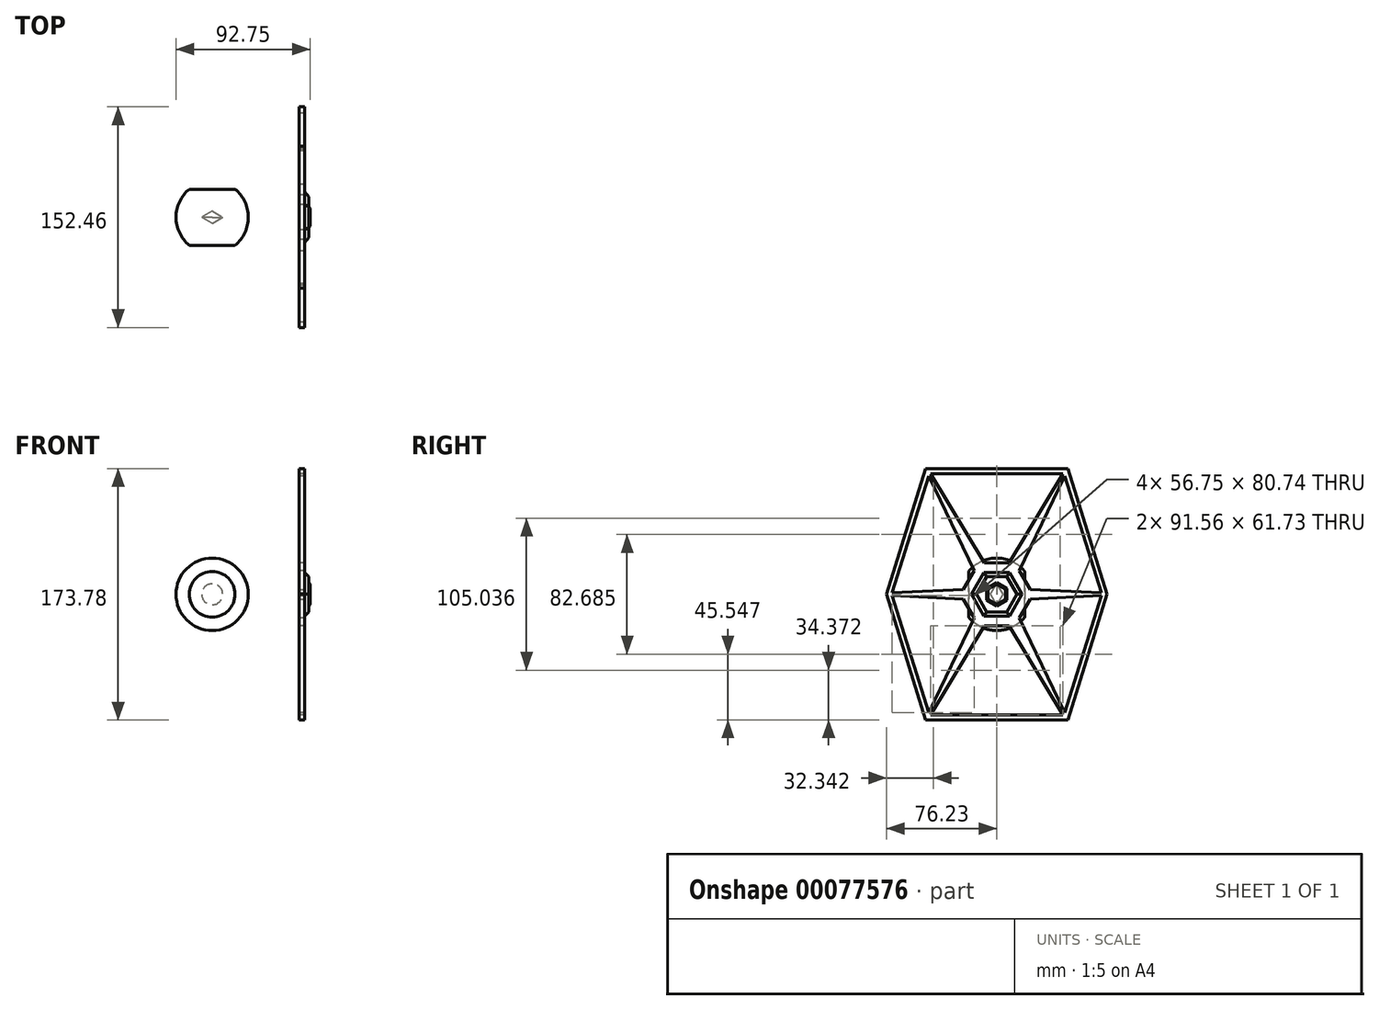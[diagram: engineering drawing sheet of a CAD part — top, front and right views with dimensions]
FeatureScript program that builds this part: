
annotation { "Feature Type Name" : "Feature", "Feature Type Description" : "" }
export const myFeature = defineFeature(function(context is Context, id is Id, definition is map)
    precondition{}
    {
        {
            var Q0;
            Q0=qCreatedBy(makeId("Right.planeOp"),FACE);
            var sketch = newSketch(context, id + "F0", { "sketchPlane" : qUnion([Q0])});
            skLineSegment(sketch, "E0", {"start": v(-19.38, 15.8) * mm, "end": v(-19.38, 0) * mm});
            skLineSegment(sketch, "E1", {"start": v(19.38, 15.8) * mm, "end": v(19.38, 0) * mm});
            skArc(sketch, "E2.trimOffspring", {"start": v(19.38, 15.8) * mm, "mid": v(0, 25) * mm, "end": v(-19.38, 15.8) * mm});
            skPoint(sketch, "E3.end.orphan", {"position": v(19.38, -15.72) * mm});
            skPoint(sketch, "E3.start.orphan", {"position": v(-19.38, -16.12) * mm});
            skLineSegment(sketch, "E4", {"start": v(0, 0) * mm, "end": v(0, 86.89) * mm, "construction": true});
            skPoint(sketch, "E4.endSnap0", {"position": v(0, 25) * mm});
            skLineSegment(sketch, "E5", {"start": v(0, 86.89) * mm, "end": v(49.08, 86.89) * mm});
            skLineSegment(sketch, "E6", {"start": v(49.08, 86.89) * mm, "end": v(76.23, 0) * mm});
            skLineSegment(sketch, "E7", {"start": v(0, 83.39) * mm, "end": v(45.78, 83.39) * mm});
            skLineSegment(sketch, "E8", {"start": v(45.78, 83.39) * mm, "end": v(-4.38, 0) * mm});
            skLineSegment(sketch, "E9.0", {"start": v(47.03, 81.71) * mm, "end": v(72.57, 0) * mm});
            skLineSegment(sketch, "E10", {"start": v(76.23, 0) * mm, "end": v(0, 0) * mm, "construction": true});
            skLineSegment(sketch, "E11", {"start": v(0, 0) * mm, "end": v(-19.38, 0) * mm});
            skLineSegment(sketch, "E12", {"start": v(0, 0) * mm, "end": v(19.38, 0) * mm});
            skPoint(sketch, "E13.orphan", {"position": v(19.38, 0.04) * mm});
            skPoint(sketch, "E14.orphan", {"position": v(-19.38, -0.16) * mm});
            skLineSegment(sketch, "E15", {"start": v(47.03, 81.71) * mm, "end": v(7.57, 0) * mm});
            skLineSegment(sketch, "E16.MirrorCS", {"start": v(0, 86.89) * mm, "end": v(-49.08, 86.89) * mm});
            skLineSegment(sketch, "E17.MirrorCS", {"start": v(0, 83.39) * mm, "end": v(-45.78, 83.39) * mm});
            skLineSegment(sketch, "E18.MirrorCS", {"start": v(-49.08, 86.89) * mm, "end": v(-76.23, 0) * mm});
            skLineSegment(sketch, "E19.MirrorCS", {"start": v(-47.03, 81.71) * mm, "end": v(-72.57, 0) * mm});
            skLineSegment(sketch, "E20.MirrorCS", {"start": v(-45.78, 83.39) * mm, "end": v(4.38, 0) * mm});
            skLineSegment(sketch, "E21.MirrorCS", {"start": v(-47.03, 81.71) * mm, "end": v(-7.57, 0) * mm});
            skLineSegment(sketch, "E22.MirrorCS", {"start": v(-76.23, 0) * mm, "end": v(0, 0) * mm, "construction": true});
            skLineSegment(sketch, "E23.MirrorCS", {"start": v(47.03, -81.71) * mm, "end": v(72.57, 0) * mm});
            skLineSegment(sketch, "E24.MirrorCS", {"start": v(49.08, -86.89) * mm, "end": v(76.23, 0) * mm});
            skLineSegment(sketch, "E25.MirrorCS", {"start": v(47.03, -81.71) * mm, "end": v(7.57, 0) * mm});
            skLineSegment(sketch, "E26.MirrorCS", {"start": v(45.78, -83.39) * mm, "end": v(-4.38, 0) * mm});
            skLineSegment(sketch, "E27.MirrorCS", {"start": v(0, -83.39) * mm, "end": v(45.78, -83.39) * mm});
            skLineSegment(sketch, "E28.MirrorCS", {"start": v(0, -86.89) * mm, "end": v(49.08, -86.89) * mm});
            skLineSegment(sketch, "E29.MirrorCS", {"start": v(0, -86.89) * mm, "end": v(-49.08, -86.89) * mm});
            skLineSegment(sketch, "E30.MirrorCS", {"start": v(0, -83.39) * mm, "end": v(-45.78, -83.39) * mm});
            skLineSegment(sketch, "E31.MirrorCS", {"start": v(-45.78, -83.39) * mm, "end": v(4.38, 0) * mm});
            skLineSegment(sketch, "E32.MirrorCS", {"start": v(-47.03, -81.71) * mm, "end": v(-7.57, 0) * mm});
            skLineSegment(sketch, "E33.MirrorCS", {"start": v(-47.03, -81.71) * mm, "end": v(-72.57, 0) * mm});
            skLineSegment(sketch, "E34.MirrorCS", {"start": v(-49.08, -86.89) * mm, "end": v(-76.23, 0) * mm});
            skSolve(sketch);
        }
        {
            var Q0;
            {var subQ6=sQuery(id+"F0.wireOp",EDGE,"E0");Q0=makeQuery(id+"F0.imprint","IMPRINT",FACE,{"disambiguationData":[TD([[makeQuery(id+"F0.imprint","IMPRINT",EDGE,{"derivedFrom":subQ6}),1.0]])]});}
            var Q1;
            {var subQ6=sQuery(id+"F0.wireOp",EDGE,"E20.MirrorCS");var subQ8=sQuery(id+"F0.wireOp",EDGE,"E2.trimOffspring");var subQ9=makeQuery(id+"F0.imprint","INTERSECT",VERTEX,{"derivedFrom":[subQ8,subQ6]});Q1=makeQuery(id+"F0.imprint","IMPRINT",FACE,{"disambiguationData":[TD([[makeQuery(id+"F0.imprint","IMPRINT",EDGE,{"disambiguationData":[TD([[subQ9,-1.0]])],"derivedFrom":subQ8}),1.0]])]});}
            var Q2;
            {var subQ0=sQuery(id+"F0.wireOp",EDGE,"E8");var subQ1=sQuery(id+"F0.wireOp",EDGE,"E2.trimOffspring");var subQ2=makeQuery(id+"F0.imprint","INTERSECT",VERTEX,{"derivedFrom":[subQ1,subQ0]});Q2=makeQuery(id+"F0.imprint","IMPRINT",FACE,{"disambiguationData":[TD([[makeQuery(id+"F0.imprint","IMPRINT",EDGE,{"disambiguationData":[TD([[subQ2,-1.0]])],"derivedFrom":subQ1}),1.0]])]});}
            var Q3;
            {var subQ1=sQuery(id+"F0.wireOp",EDGE,"E2.trimOffspring");var subQ5=sQuery(id+"F0.wireOp",EDGE,"E15");var subQ10=makeQuery(id+"F0.imprint","INTERSECT",VERTEX,{"derivedFrom":[subQ1,subQ5]});Q3=makeQuery(id+"F0.imprint","IMPRINT",FACE,{"disambiguationData":[TD([[makeQuery(id+"F0.imprint","IMPRINT",EDGE,{"disambiguationData":[TD([[subQ10,-1.0]])],"derivedFrom":subQ1}),1.0]])]});}
            var Q4;
            {var subQ0=sQuery(id+"F0.wireOp",EDGE,"E1");Q4=makeQuery(id+"F0.imprint","IMPRINT",FACE,{"disambiguationData":[TD([[makeQuery(id+"F0.imprint","IMPRINT",EDGE,{"derivedFrom":subQ0}),-1.0]])]});}
            var Q5;
            {var subQ5=sQuery(id+"F0.wireOp",EDGE,"bc8b1be5-37c6-41ea-9046-8c1789669ef70.MirrorCS");var subQ7=sQuery(id+"F0.wireOp",EDGE,"E8");var subQ9=makeQuery(id+"F0.imprint","INTERSECT",VERTEX,{"derivedFrom":[subQ7,subQ5]});Q5=makeQuery(id+"F0.imprint","IMPRINT",FACE,{"disambiguationData":[TD([[makeQuery(id+"F0.imprint","IMPRINT",EDGE,{"disambiguationData":[TD([[subQ9,1.0]])],"derivedFrom":subQ7}),1.0]])]});}
            var Q6;
            Q6=sQuery(id+"F0.wireOp",EDGE,"E12");
            revolve(context, id + "F1", {"entities" : qUnion([Q0, Q1, Q2, Q3, Q4, Q5]), "axis" : qUnion([Q6]), "revolveType" : RevolveType.FULL});
        }
        {
            var Q0;
            Q0=makeQuery(id+"F0.imprint","IMPRINT",FACE,{"disambiguationData":[TD([[makeQuery(id+"F0.imprint","IMPRINT",EDGE,{"derivedFrom":sQuery(id+"F0.wireOp",EDGE,"E5")}),-1.0]])]});
            var Q1;
            {var subQ0=sQuery(id+"F0.wireOp",EDGE,"E20.MirrorCS");var subQ1=sQuery(id+"F0.wireOp",EDGE,"E2.trimOffspring");var subQ2=makeQuery(id+"F0.imprint","INTERSECT",VERTEX,{"derivedFrom":[subQ1,subQ0]});Q1=makeQuery(id+"F0.imprint","IMPRINT",FACE,{"disambiguationData":[TD([[makeQuery(id+"F0.imprint","IMPRINT",EDGE,{"disambiguationData":[TD([[subQ2,-1.0]])],"derivedFrom":subQ1}),1.0]])]});}
            var Q2;
            {var subQ0=sQuery(id+"F0.wireOp",EDGE,"E15");var subQ3=sQuery(id+"F0.wireOp",EDGE,"E2.trimOffspring");var subQ4=makeQuery(id+"F0.imprint","INTERSECT",VERTEX,{"derivedFrom":[subQ3,subQ0]});Q2=makeQuery(id+"F0.imprint","IMPRINT",FACE,{"disambiguationData":[TD([[makeQuery(id+"F0.imprint","IMPRINT",EDGE,{"disambiguationData":[TD([[subQ4,-1.0]])],"derivedFrom":subQ3}),1.0]])]});}
            var Q3;
            {var subQ1=sQuery(id+"F0.wireOp",EDGE,"E8");var subQ3=sQuery(id+"F0.wireOp",EDGE,"E20.MirrorCS");var subQ4=makeQuery(id+"F0.imprint","INTERSECT",VERTEX,{"derivedFrom":[subQ1,subQ3]});Q3=makeQuery(id+"F0.imprint","IMPRINT",FACE,{"disambiguationData":[TD([[makeQuery(id+"F0.imprint","IMPRINT",EDGE,{"disambiguationData":[TD([[subQ4,-1.0]])],"derivedFrom":subQ1}),1.0]])]});}
            var Q4;
            {var subQ1=sQuery(id+"F0.wireOp",EDGE,"E11");var subQ3=sQuery(id+"F0.wireOp",EDGE,"E12");var subQ4=makeQuery(id+"F0.imprint","INTERSECT",VERTEX,{"derivedFrom":[subQ1,subQ3]});Q4=makeQuery(id+"F0.imprint","IMPRINT",FACE,{"disambiguationData":[TD([[makeQuery(id+"F0.imprint","IMPRINT",EDGE,{"disambiguationData":[TD([[subQ4,-1.0]])],"derivedFrom":subQ1}),1.0]])]});}
            extrude(context, id + "F2", {"entities" : qUnion([Q0, Q1, Q2, Q3, Q4]), "depth" : 63.75 * mm, "hasSecondDirection" : true, "secondDirectionOppositeDirection" : false, "secondDirectionDepth" : 60.25 * mm});
        }
        {
            var Q0;
            Q0=makeQuery(id+"F2.opExtrude","CAP_FACE",FACE,{"disambiguationData":[OSD([sQuery(id+"F0.wireOp",EDGE,"E5"),sQuery(id+"F0.wireOp",EDGE,"E6"),sQuery(id+"F0.wireOp",EDGE,"E7"),sQuery(id+"F0.wireOp",EDGE,"E8"),sQuery(id+"F0.wireOp",EDGE,"E9.0"),sQuery(id+"F0.wireOp",EDGE,"E15"),sQuery(id+"F0.wireOp",EDGE,"E16.MirrorCS"),sQuery(id+"F0.wireOp",EDGE,"E17.MirrorCS"),sQuery(id+"F0.wireOp",EDGE,"E18.MirrorCS"),sQuery(id+"F0.wireOp",EDGE,"E19.MirrorCS"),sQuery(id+"F0.wireOp",EDGE,"E20.MirrorCS"),sQuery(id+"F0.wireOp",EDGE,"E21.MirrorCS"),sQuery(id+"F0.wireOp",EDGE,"E23.MirrorCS"),sQuery(id+"F0.wireOp",EDGE,"E24.MirrorCS"),sQuery(id+"F0.wireOp",EDGE,"E25.MirrorCS"),sQuery(id+"F0.wireOp",EDGE,"E26.MirrorCS"),sQuery(id+"F0.wireOp",EDGE,"E27.MirrorCS"),sQuery(id+"F0.wireOp",EDGE,"E28.MirrorCS"),sQuery(id+"F0.wireOp",EDGE,"E29.MirrorCS"),sQuery(id+"F0.wireOp",EDGE,"E30.MirrorCS"),sQuery(id+"F0.wireOp",EDGE,"E31.MirrorCS"),sQuery(id+"F0.wireOp",EDGE,"E32.MirrorCS"),sQuery(id+"F0.wireOp",EDGE,"E33.MirrorCS"),sQuery(id+"F0.wireOp",EDGE,"E34.MirrorCS")])],"isStart":false});
            var sketch = newSketch(context, id + "F3", { "sketchPlane" : qUnion([Q0])});
            skCircle(sketch, "E35.cCircle", {"center": v(0, 0) * mm, "radius": 25 * mm, "construction": true});
            skLineSegment(sketch, "E35.0", {"start": v(25, 0) * mm, "end": v(12.5, -21.65) * mm});
            skLineSegment(sketch, "E35.1", {"start": v(12.5, -21.65) * mm, "end": v(-12.5, -21.65) * mm});
            skLineSegment(sketch, "E35.2", {"start": v(-12.5, -21.65) * mm, "end": v(-25, 0) * mm});
            skLineSegment(sketch, "E35.3", {"start": v(-25, 0) * mm, "end": v(-12.5, 21.65) * mm});
            skLineSegment(sketch, "E35.4", {"start": v(-12.5, 21.65) * mm, "end": v(12.5, 21.65) * mm});
            skLineSegment(sketch, "E35.5", {"start": v(12.5, 21.65) * mm, "end": v(25, 0) * mm});
            skLineSegment(sketch, "E36", {"start": v(-72.26, 0.97) * mm, "end": v(0, 4.35) * mm});
            skLineSegment(sketch, "E37.MirrorCS", {"start": v(72.26, 0.97) * mm, "end": v(0, 4.35) * mm});
            skLineSegment(sketch, "E38.MirrorCS", {"start": v(72.26, -0.97) * mm, "end": v(0, -4.35) * mm});
            skLineSegment(sketch, "E39.MirrorCS", {"start": v(-72.26, -0.97) * mm, "end": v(0, -4.35) * mm});
            skSolve(sketch);
        }
        {
            var Q0;
            Q0 = qSketchRegion(id + "F3", true);
            var Q1;
            {var subQ3=sQuery(id+"F3.wireOp",EDGE,"E35.2");var subQ8=sQuery(id+"F3.wireOp",EDGE,"E35.3");var subQ11=makeQuery(id+"F3.imprint","INTERSECT",VERTEX,{"derivedFrom":[subQ3,subQ8]});Q1=makeQuery(id+"F3.imprint","IMPRINT",FACE,{"disambiguationData":[TD([[makeQuery(id+"F3.imprint","IMPRINT",EDGE,{"disambiguationData":[TD([[subQ11,1.0]])],"derivedFrom":subQ3}),1.0]])]});}
            var Q2;
            {var subQ3=sQuery(id+"F3.wireOp",EDGE,"E35.0");var subQ8=sQuery(id+"F3.wireOp",EDGE,"E35.5");var subQ10=makeQuery(id+"F3.imprint","INTERSECT",VERTEX,{"derivedFrom":[subQ3,subQ8]});Q2=makeQuery(id+"F3.imprint","IMPRINT",FACE,{"disambiguationData":[TD([[makeQuery(id+"F3.imprint","IMPRINT",EDGE,{"disambiguationData":[TD([[subQ10,-1.0]])],"derivedFrom":subQ3}),1.0]])]});}
            var Q3;
            Q3=makeQuery(id+"F2.opExtrude","CAP_FACE",FACE,{"disambiguationData":[OSD([sQuery(id+"F0.wireOp",EDGE,"E5"),sQuery(id+"F0.wireOp",EDGE,"E6"),sQuery(id+"F0.wireOp",EDGE,"E7"),sQuery(id+"F0.wireOp",EDGE,"E8"),sQuery(id+"F0.wireOp",EDGE,"E9.0"),sQuery(id+"F0.wireOp",EDGE,"E15"),sQuery(id+"F0.wireOp",EDGE,"E16.MirrorCS"),sQuery(id+"F0.wireOp",EDGE,"E17.MirrorCS"),sQuery(id+"F0.wireOp",EDGE,"E18.MirrorCS"),sQuery(id+"F0.wireOp",EDGE,"E19.MirrorCS"),sQuery(id+"F0.wireOp",EDGE,"E20.MirrorCS"),sQuery(id+"F0.wireOp",EDGE,"E21.MirrorCS"),sQuery(id+"F0.wireOp",EDGE,"E23.MirrorCS"),sQuery(id+"F0.wireOp",EDGE,"E24.MirrorCS"),sQuery(id+"F0.wireOp",EDGE,"E25.MirrorCS"),sQuery(id+"F0.wireOp",EDGE,"E26.MirrorCS"),sQuery(id+"F0.wireOp",EDGE,"E27.MirrorCS"),sQuery(id+"F0.wireOp",EDGE,"E28.MirrorCS"),sQuery(id+"F0.wireOp",EDGE,"E29.MirrorCS"),sQuery(id+"F0.wireOp",EDGE,"E30.MirrorCS"),sQuery(id+"F0.wireOp",EDGE,"E31.MirrorCS"),sQuery(id+"F0.wireOp",EDGE,"E32.MirrorCS"),sQuery(id+"F0.wireOp",EDGE,"E33.MirrorCS"),sQuery(id+"F0.wireOp",EDGE,"E34.MirrorCS")])],"isStart":true});
            extrude(context, id + "F4", {"entities" : qUnion([Q0, Q1, Q2]), "operationType" : NewBodyOperationType.ADD, "endBound" : BoundingType.UP_TO_SURFACE, "oppositeDirection" : true, "endBoundEntityFace" : qUnion([Q3]), "depth" : 25 * mm});
        }
        {
            var Q0;
            {var subQ0=sQuery(id+"F0.wireOp",EDGE,"E33.MirrorCS");var subQ1=sQuery(id+"F0.wireOp",EDGE,"E23.MirrorCS");var subQ2=sQuery(id+"F0.wireOp",EDGE,"E19.MirrorCS");var subQ3=sQuery(id+"F0.wireOp",EDGE,"E9.0");Q0=makeQuery(id+"F4.boolean.opBoolean","MERGE",FACE,{"derivedFrom":[makeQuery(id+"F2.opExtrude","CAP_FACE",FACE,{"disambiguationData":[OSD([sQuery(id+"F0.wireOp",EDGE,"E5"),sQuery(id+"F0.wireOp",EDGE,"E6"),sQuery(id+"F0.wireOp",EDGE,"E7"),sQuery(id+"F0.wireOp",EDGE,"E8"),subQ3,sQuery(id+"F0.wireOp",EDGE,"E15"),sQuery(id+"F0.wireOp",EDGE,"E16.MirrorCS"),sQuery(id+"F0.wireOp",EDGE,"E17.MirrorCS"),sQuery(id+"F0.wireOp",EDGE,"E18.MirrorCS"),subQ2,sQuery(id+"F0.wireOp",EDGE,"E20.MirrorCS"),sQuery(id+"F0.wireOp",EDGE,"E21.MirrorCS"),subQ1,sQuery(id+"F0.wireOp",EDGE,"E24.MirrorCS"),sQuery(id+"F0.wireOp",EDGE,"E25.MirrorCS"),sQuery(id+"F0.wireOp",EDGE,"E26.MirrorCS"),sQuery(id+"F0.wireOp",EDGE,"E27.MirrorCS"),sQuery(id+"F0.wireOp",EDGE,"E28.MirrorCS"),sQuery(id+"F0.wireOp",EDGE,"E29.MirrorCS"),sQuery(id+"F0.wireOp",EDGE,"E30.MirrorCS"),sQuery(id+"F0.wireOp",EDGE,"E31.MirrorCS"),sQuery(id+"F0.wireOp",EDGE,"E32.MirrorCS"),subQ0,sQuery(id+"F0.wireOp",EDGE,"E34.MirrorCS")])],"isStart":false}),makeQuery(id+"F4.opExtrude","CAP_FACE",FACE,{"disambiguationData":[OSD([subQ3,subQ2,subQ1,subQ0,sQuery(id+"F3.wireOp",EDGE,"E35.0"),sQuery(id+"F3.wireOp",EDGE,"E35.1"),sQuery(id+"F3.wireOp",EDGE,"E35.2"),sQuery(id+"F3.wireOp",EDGE,"E35.3"),sQuery(id+"F3.wireOp",EDGE,"E35.4"),sQuery(id+"F3.wireOp",EDGE,"E35.5"),sQuery(id+"F3.wireOp",EDGE,"E36"),sQuery(id+"F3.wireOp",EDGE,"E37.MirrorCS"),sQuery(id+"F3.wireOp",EDGE,"E38.MirrorCS"),sQuery(id+"F3.wireOp",EDGE,"E39.MirrorCS")])],"isStart":true})]});}
            var sketch = newSketch(context, id + "F5", { "sketchPlane" : qUnion([Q0])});
            skLineSegment(sketch, "E40", {"start": v(-90.67, 15.2) * mm, "end": v(31.13, 15.2) * mm, "construction": true});
            skLineSegment(sketch, "E41", {"start": v(-87.14, 2.9) * mm, "end": v(-87.14, 20.1) * mm, "construction": true});
            skCircle(sketch, "E42.cCircle", {"center": v(0, 0) * mm, "radius": 15.2 * mm, "construction": true});
            skLineSegment(sketch, "E42.0", {"start": v(-8.77, 15.2) * mm, "end": v(8.77, 15.2) * mm});
            skLineSegment(sketch, "E42.1", {"start": v(8.77, 15.2) * mm, "end": v(17.55, 0) * mm});
            skLineSegment(sketch, "E42.2", {"start": v(17.55, 0) * mm, "end": v(8.77, -15.2) * mm});
            skLineSegment(sketch, "E42.3", {"start": v(8.77, -15.2) * mm, "end": v(-8.77, -15.2) * mm});
            skLineSegment(sketch, "E42.4", {"start": v(-8.77, -15.2) * mm, "end": v(-17.55, 0) * mm});
            skLineSegment(sketch, "E42.5", {"start": v(-17.55, 0) * mm, "end": v(-8.77, 15.2) * mm});
            skPoint(sketch, "E42.0.midPoint", {"position": v(0, 15.2) * mm});
            skSolve(sketch);
        }
        {
            var Q0;
            Q0=makeQuery(id+"F5.imprint","IMPRINT",FACE,{"disambiguationData":[TD([[makeQuery(id+"F5.imprint","IMPRINT",EDGE,{"derivedFrom":sQuery(id+"F5.wireOp",EDGE,"E42.0")}),-1.0]])]});
            extrude(context, id + "F6", {"entities" : qUnion([Q0]), "operationType" : NewBodyOperationType.ADD, "depth" : 3 * mm});
        }
        {
            var Q0;
            Q0=makeQuery(id+"F6.opExtrude","CAP_EDGE",EDGE,{"disambiguationData":[OSD([sQuery(id+"F5.wireOp",EDGE,"E42.5")])],"isStart":false});
            var Q1;
            Q1=makeQuery(id+"F6.opExtrude","CAP_EDGE",EDGE,{"disambiguationData":[OSD([sQuery(id+"F5.wireOp",EDGE,"E42.0")])],"isStart":false});
            var Q2;
            Q2=makeQuery(id+"F6.opExtrude","CAP_EDGE",EDGE,{"disambiguationData":[OSD([sQuery(id+"F5.wireOp",EDGE,"E42.1")])],"isStart":false});
            var Q3;
            Q3=makeQuery(id+"F6.opExtrude","CAP_EDGE",EDGE,{"disambiguationData":[OSD([sQuery(id+"F5.wireOp",EDGE,"E42.2")])],"isStart":false});
            var Q4;
            Q4=makeQuery(id+"F6.opExtrude","CAP_EDGE",EDGE,{"disambiguationData":[OSD([sQuery(id+"F5.wireOp",EDGE,"E42.3")])],"isStart":false});
            var Q5;
            Q5=makeQuery(id+"F6.opExtrude","CAP_EDGE",EDGE,{"disambiguationData":[OSD([sQuery(id+"F5.wireOp",EDGE,"E42.4")])],"isStart":false});
            chamfer(context, id + "F7", {"entities" : qUnion([Q0, Q1, Q2, Q3, Q4, Q5]), "width" : 3 * mm, "tangentPropagation" : true});
        }
        {
            var Q0;
            Q0=makeQuery(id+"F6.opExtrude","CAP_FACE",FACE,{"disambiguationData":[OSD([sQuery(id+"F5.wireOp",EDGE,"E42.0"),sQuery(id+"F5.wireOp",EDGE,"E42.1"),sQuery(id+"F5.wireOp",EDGE,"E42.2"),sQuery(id+"F5.wireOp",EDGE,"E42.3"),sQuery(id+"F5.wireOp",EDGE,"E42.4"),sQuery(id+"F5.wireOp",EDGE,"E42.5")])],"isStart":false});
            var sketch = newSketch(context, id + "F8", { "sketchPlane" : qUnion([Q0])});
            skLineSegment(sketch, "E43", {"start": v(-88.09, 8.16) * mm, "end": v(4.83, 8.16) * mm, "construction": true});
            skCircle(sketch, "E44.cCircle", {"center": v(0, 0) * mm, "radius": 7.11 * mm, "construction": true});
            skLineSegment(sketch, "E44.0", {"start": v(7.11, 4.1) * mm, "end": v(7.11, -4.1) * mm});
            skLineSegment(sketch, "E44.1", {"start": v(7.11, -4.1) * mm, "end": v(0, -8.21) * mm});
            skLineSegment(sketch, "E44.2", {"start": v(0, -8.21) * mm, "end": v(-7.11, -4.1) * mm});
            skLineSegment(sketch, "E44.3", {"start": v(-7.11, -4.1) * mm, "end": v(-7.11, 4.1) * mm});
            skLineSegment(sketch, "E44.4", {"start": v(-7.11, 4.1) * mm, "end": v(0, 8.21) * mm});
            skLineSegment(sketch, "E44.5", {"start": v(0, 8.21) * mm, "end": v(7.11, 4.1) * mm});
            skPoint(sketch, "E44.0.midPoint", {"position": v(7.11, 0) * mm});
            skSolve(sketch);
        }
        {
            var Q0;
            Q0=makeQuery(id+"F8.imprint","IMPRINT",FACE,{"disambiguationData":[TD([[makeQuery(id+"F8.imprint","IMPRINT",EDGE,{"derivedFrom":sQuery(id+"F8.wireOp",EDGE,"E44.0")}),-1.0]])]});
            extrude(context, id + "F9", {"entities" : qUnion([Q0]), "operationType" : NewBodyOperationType.ADD, "depth" : 1 * mm});
        }
        {
            var Q0;
            Q0=makeQuery(id+"F9.opExtrude","CAP_EDGE",EDGE,{"disambiguationData":[OSD([sQuery(id+"F8.wireOp",EDGE,"E44.4")])],"isStart":false});
            var Q1;
            Q1=makeQuery(id+"F9.opExtrude","CAP_EDGE",EDGE,{"disambiguationData":[OSD([sQuery(id+"F8.wireOp",EDGE,"E44.5")])],"isStart":false});
            var Q2;
            Q2=makeQuery(id+"F9.opExtrude","CAP_EDGE",EDGE,{"disambiguationData":[OSD([sQuery(id+"F8.wireOp",EDGE,"E44.0")])],"isStart":false});
            var Q3;
            Q3=makeQuery(id+"F9.opExtrude","CAP_EDGE",EDGE,{"disambiguationData":[OSD([sQuery(id+"F8.wireOp",EDGE,"E44.1")])],"isStart":false});
            var Q4;
            Q4=makeQuery(id+"F9.opExtrude","CAP_EDGE",EDGE,{"disambiguationData":[OSD([sQuery(id+"F8.wireOp",EDGE,"E44.2")])],"isStart":false});
            var Q5;
            Q5=makeQuery(id+"F9.opExtrude","CAP_EDGE",EDGE,{"disambiguationData":[OSD([sQuery(id+"F8.wireOp",EDGE,"E44.3")])],"isStart":false});
            chamfer(context, id + "F10", {"entities" : qUnion([Q0, Q1, Q2, Q3, Q4, Q5]), "width" : 1 * mm, "tangentPropagation" : true});
        }
    });
